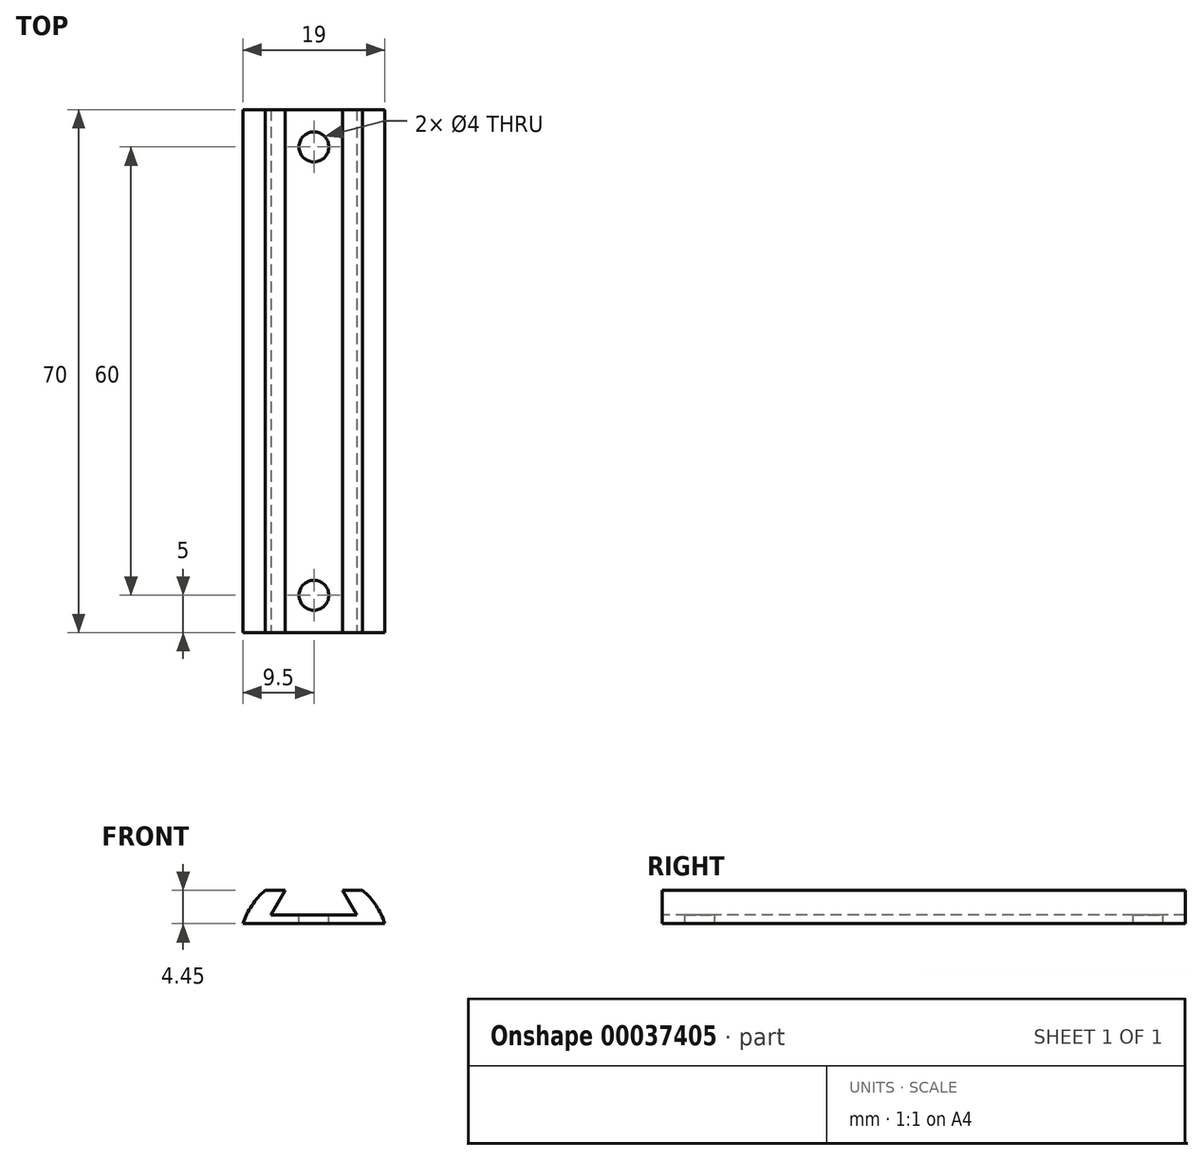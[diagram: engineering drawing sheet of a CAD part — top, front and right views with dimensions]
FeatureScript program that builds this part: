
annotation { "Feature Type Name" : "Feature", "Feature Type Description" : "" }
export const myFeature = defineFeature(function(context is Context, id is Id, definition is map)
    precondition{}
    {
        {
            var Q0;
            Q0=qCreatedBy(makeId("Front.planeOp"),FACE);
            var sketch = newSketch(context, id + "F0", { "sketchPlane" : qUnion([Q0])});
            skArc(sketch, "E0", {"start": v(9.5, 3.12) * mm, "mid": v(8.32, 5.55) * mm, "end": v(6.53, 7.57) * mm});
            skLineSegment(sketch, "E1", {"start": v(-9.5, 3.12) * mm, "end": v(9.5, 3.12) * mm});
            skPoint(sketch, "E2.endSnap0", {"position": v(0, 3.12) * mm});
            skLineSegment(sketch, "E3", {"start": v(0, 4.27) * mm, "end": v(-5.74, 4.27) * mm});
            skLineSegment(sketch, "E4", {"start": v(-5.74, 4.27) * mm, "end": v(-3.83, 7.57) * mm});
            skLineSegment(sketch, "E5", {"start": v(-3.83, 7.57) * mm, "end": v(-6.53, 7.57) * mm});
            skLineSegment(sketch, "E6.MirrorCS", {"start": v(5.74, 4.27) * mm, "end": v(3.83, 7.57) * mm});
            skLineSegment(sketch, "E7.MirrorCS", {"start": v(3.83, 7.57) * mm, "end": v(6.53, 7.57) * mm});
            skLineSegment(sketch, "E8.MirrorCS", {"start": v(0, 4.27) * mm, "end": v(5.74, 4.27) * mm});
            skArc(sketch, "E9.trimOffspring", {"start": v(-6.53, 7.57) * mm, "mid": v(-8.32, 5.55) * mm, "end": v(-9.5, 3.12) * mm});
            skSolve(sketch);
        }
        {
            var Q0;
            Q0=makeQuery(id+"F0.imprint","IMPRINT",FACE,{"disambiguationData":[TD([[makeQuery(id+"F0.imprint","IMPRINT",EDGE,{"derivedFrom":sQuery(id+"F0.wireOp",EDGE,"E0")}),1.0]])]});
            extrude(context, id + "F1", {"entities" : qUnion([Q0]), "oppositeDirection" : true, "depth" : 70 * mm});
        }
        {
            var Q0;
            Q0=makeQuery(id+"F1.opExtrude","SWEPT_FACE",FACE,{"disambiguationData":[OSD([sQuery(id+"F0.wireOp",EDGE,"E3"),sQuery(id+"F0.wireOp",EDGE,"E8.MirrorCS")])]});
            var sketch = newSketch(context, id + "F2", { "sketchPlane" : qUnion([Q0])});
            skCircle(sketch, "E10", {"center": v(0, 5) * mm, "radius": 2 * mm});
            skCircle(sketch, "E11.MirrorC", {"center": v(0, 65) * mm, "radius": 2 * mm});
            skSolve(sketch);
        }
        {
            var Q0;
            Q0=makeQuery(id+"F2.imprint","IMPRINT",FACE,{"disambiguationData":[TD([[makeQuery(id+"F2.imprint","IMPRINT",EDGE,{"derivedFrom":sQuery(id+"F2.wireOp",EDGE,"E10")}),1.0]])]});
            extrude(context, id + "F3", {"entities" : qUnion([Q0]), "operationType" : NewBodyOperationType.REMOVE, "endBound" : BoundingType.THROUGH_ALL, "oppositeDirection" : true, "depth" : 25 * mm});
        }
        {
            var Q0;
            Q0 = qSketchRegion(id + "F2", true);
            extrude(context, id + "F4", {"entities" : qUnion([Q0]), "operationType" : NewBodyOperationType.REMOVE, "endBound" : BoundingType.THROUGH_ALL, "oppositeDirection" : true, "depth" : 25 * mm});
        }
    });
